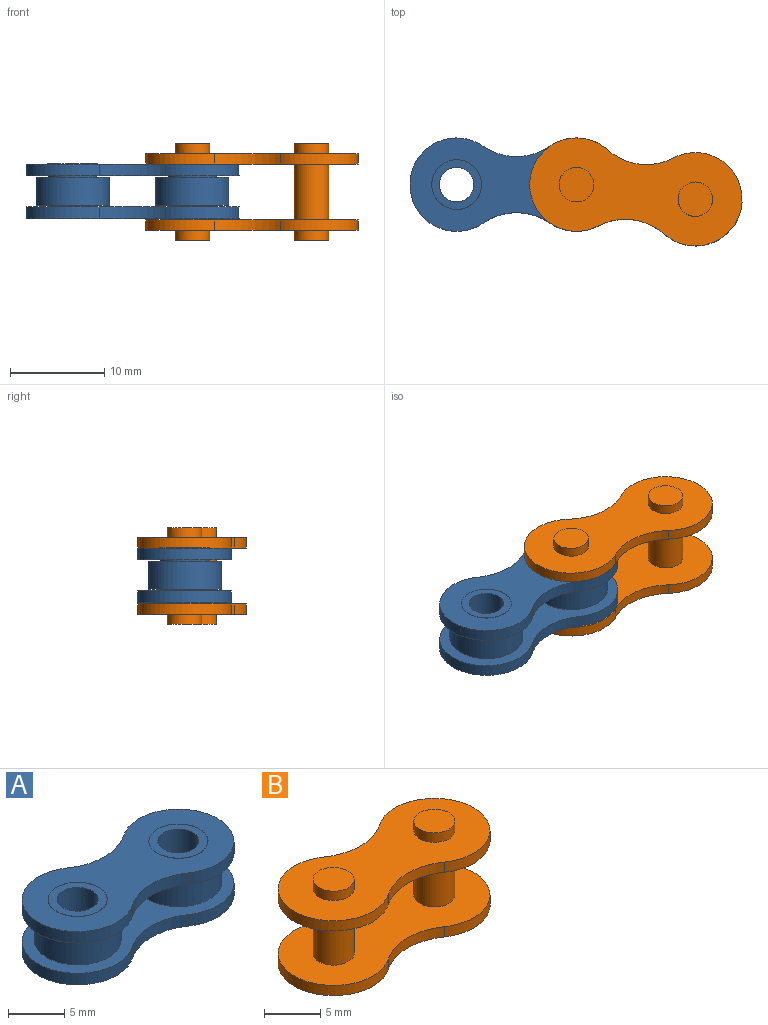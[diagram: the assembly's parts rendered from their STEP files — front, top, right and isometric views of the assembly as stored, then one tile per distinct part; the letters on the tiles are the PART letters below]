
ASSEMBLY  parts=2 mates=1
PART A: 32 faces, bbox 22.6x9.9x5.9 mm
  f0: cylinder r=2.64mm len=5.27mm, axis (0,0,1), area 2.7mm2, adj f25,f29
  f1: cylinder r=2.64mm len=5.27mm, axis (0,0,1), area 2.7mm2, adj f25,f26
  f2: cylinder r=2.64mm len=5.27mm, axis (0,0,1), area 2.7mm2, adj f13,f27
  f3: cylinder r=2.64mm len=5.27mm, axis (0,0,1), area 2.7mm2, adj f13,f30
  f4: cylinder r=2.64mm len=5.27mm, axis (0,0,1), area 0.4mm2, adj f6,f14
  f5: plane 5.27x5.27mm, normal (0,0,1), area 11.3mm2, adj f7,f8
  f6: plane 5.27x5.27mm, normal (0,0,-1), area 11.3mm2, adj f4,f8
  f7: cylinder r=2.64mm len=5.27mm, axis (0,0,1), area 0.4mm2, adj f5,f24
  f8: cylinder r=1.83mm len=5.85mm, axis (0,0,1), area 67.3mm2, adj f5,f6
  f9: cylinder r=4.95mm len=9.9mm, axis (0,0,-1), area 26.9mm2, adj f10,f12,f13,f14
  f10: cylinder r=6.22mm len=7.07mm, axis (0,0,-1), area 9.4mm2, adj f9,f11,f13,f14
  f11: cylinder r=4.95mm len=9.9mm, axis (0,0,-1), area 26.9mm2, adj f10,f12,f13,f14
  f12: cylinder r=6.22mm len=7.07mm, axis (0,0,-1), area 9.4mm2, adj f9,f11,f13,f14
  f13: plane 22.6x9.9mm, normal (0,0,1), area 132.9mm2, adj f2,f3,f9,f10,f11,f12
  f14: plane 22.6x9.9mm, normal (0,0,-1), area 132.9mm2, adj f4,f9,f10,f11,f12,f15
  f15: cylinder r=2.64mm len=5.27mm, axis (0,0,1), area 0.4mm2, adj f14,f17
  f16: plane 5.27x5.27mm, normal (0,0,1), area 11.3mm2, adj f18,f19
  f17: plane 5.27x5.27mm, normal (0,0,-1), area 11.3mm2, adj f15,f19
  f18: cylinder r=2.64mm len=5.27mm, axis (0,0,1), area 0.4mm2, adj f16,f24
  f19: cylinder r=1.83mm len=5.85mm, axis (0,0,1), area 67.3mm2, adj f16,f17
  f20: cylinder r=4.95mm len=9.9mm, axis (0,0,-1), area 26.9mm2, adj f21,f23,f24,f25
  f21: cylinder r=6.22mm len=7.07mm, axis (0,0,-1), area 9.4mm2, adj f20,f22,f24,f25
  f22: cylinder r=4.95mm len=9.9mm, axis (0,0,-1), area 26.9mm2, adj f21,f23,f24,f25
  f23: cylinder r=6.22mm len=7.07mm, axis (0,0,-1), area 9.4mm2, adj f20,f22,f24,f25
  f24: plane 22.6x9.9mm, normal (0,0,1), area 132.9mm2, adj f7,f18,f20,f21,f22,f23
  f25: plane 22.6x9.9mm, normal (0,0,-1), area 132.9mm2, adj f0,f1,f20,f21,f22,f23
  f26: plane 7.75x7.75mm, normal (0,0,1), area 25.4mm2, adj f1,f28
  f27: plane 7.75x7.75mm, normal (0,0,-1), area 25.4mm2, adj f2,f28
  f28: cylinder r=3.88mm len=7.75mm, axis (0,0,1), area 72.3mm2, adj f26,f27
  f29: plane 7.75x7.75mm, normal (0,0,1), area 25.4mm2, adj f0,f31
  f30: plane 7.75x7.75mm, normal (0,0,-1), area 25.4mm2, adj f3,f31
  f31: cylinder r=3.88mm len=7.75mm, axis (0,0,1), area 72.3mm2, adj f29,f30
PART B: 22 faces, bbox 22.6x9.9x10.2 mm
  f0: cylinder r=4.95mm len=9.9mm, axis (0,0,-1), area 24mm2, adj f1,f3,f4,f5
  f1: cylinder r=6.22mm len=7.07mm, axis (0,0,-1), area 8.4mm2, adj f0,f2,f4,f5
  f2: cylinder r=4.95mm len=9.9mm, axis (0,0,-1), area 24mm2, adj f1,f3,f4,f5
  f3: cylinder r=6.22mm len=7.07mm, axis (0,0,-1), area 8.4mm2, adj f0,f2,f4,f5
  f4: plane 22.6x9.9mm, normal (0,0,1), area 155.5mm2, adj f0,f1,f2,f3,f8,f21
  f5: plane 22.6x9.9mm, normal (0,0,-1), area 155.5mm2, adj f0,f1,f2,f3,f6,f19
  f6: cylinder r=1.83mm len=5.93mm, axis (0,0,1), area 68.2mm2, adj f5,f13
  f7: plane 3.66x3.66mm, normal (0,0,1), area 10.5mm2, adj f8
  f8: cylinder r=1.83mm len=3.66mm, axis (0,0,1), area 11.7mm2, adj f4,f7
  f9: cylinder r=4.95mm len=9.9mm, axis (0,0,-1), area 24mm2, adj f10,f12,f13,f14
  f10: cylinder r=6.22mm len=7.07mm, axis (0,0,-1), area 8.4mm2, adj f9,f11,f13,f14
  f11: cylinder r=4.95mm len=9.9mm, axis (0,0,-1), area 24mm2, adj f10,f12,f13,f14
  f12: cylinder r=6.22mm len=7.07mm, axis (0,0,-1), area 8.4mm2, adj f9,f11,f13,f14
  f13: plane 22.6x9.9mm, normal (0,0,1), area 155.5mm2, adj f6,f9,f10,f11,f12,f19
  f14: plane 22.6x9.9mm, normal (0,0,-1), area 155.5mm2, adj f9,f10,f11,f12,f15,f18
  f15: cylinder r=1.83mm len=3.66mm, axis (0,0,1), area 11.7mm2, adj f14,f16
  f16: plane 3.66x3.66mm, normal (0,0,-1), area 10.5mm2, adj f15
  f17: plane 3.66x3.66mm, normal (0,0,-1), area 10.5mm2, adj f18
  f18: cylinder r=1.83mm len=3.66mm, axis (0,0,1), area 11.7mm2, adj f14,f17
  f19: cylinder r=1.83mm len=5.93mm, axis (0,0,1), area 68.2mm2, adj f5,f13
  f20: plane 3.66x3.66mm, normal (0,0,1), area 10.5mm2, adj f21
  f21: cylinder r=1.83mm len=3.66mm, axis (0,0,1), area 11.7mm2, adj f4,f20
PLACE A t=(-0.44,1.23,0.07)mm
PLACE B rot(axis=(0,0,-1),7deg) t=(-0.35,2.78,0)mm
MATE revolute A.f0 <-> B.f0  axis (0,0,1) through (12.26,1.23,2.97)mm
